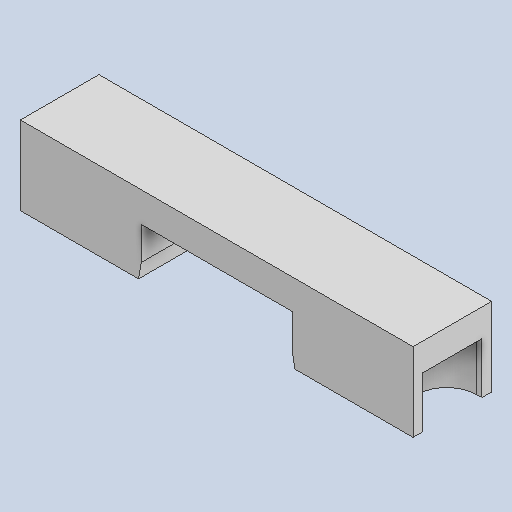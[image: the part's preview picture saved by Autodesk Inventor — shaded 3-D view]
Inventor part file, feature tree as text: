
AUTODESK INVENTOR PART (.ipt)
format: ipt  version: 2022 (Build 260153000, 153)  size: 90,624 bytes
history: native  units: in
note: dims shown in document units (in); Inventor stores cm internally (conversion verified against a paired STEP export)
features: chamfer x1
ambient origin geometry x8: Origin, YZ Plane, XZ Plane, XY Plane, X Axis, Y Axis, Z Axis, Center Point
bodies: Solid1 (feature_tree)
feature tree (1):
  chamfer  "Chamfer2"  [1 undecoded]
note: 1 required parameter value undecoded (feature->parameter linkage not recoverable at this tier; creation-order binding heuristic only, values carry confidence <= 0.55)
